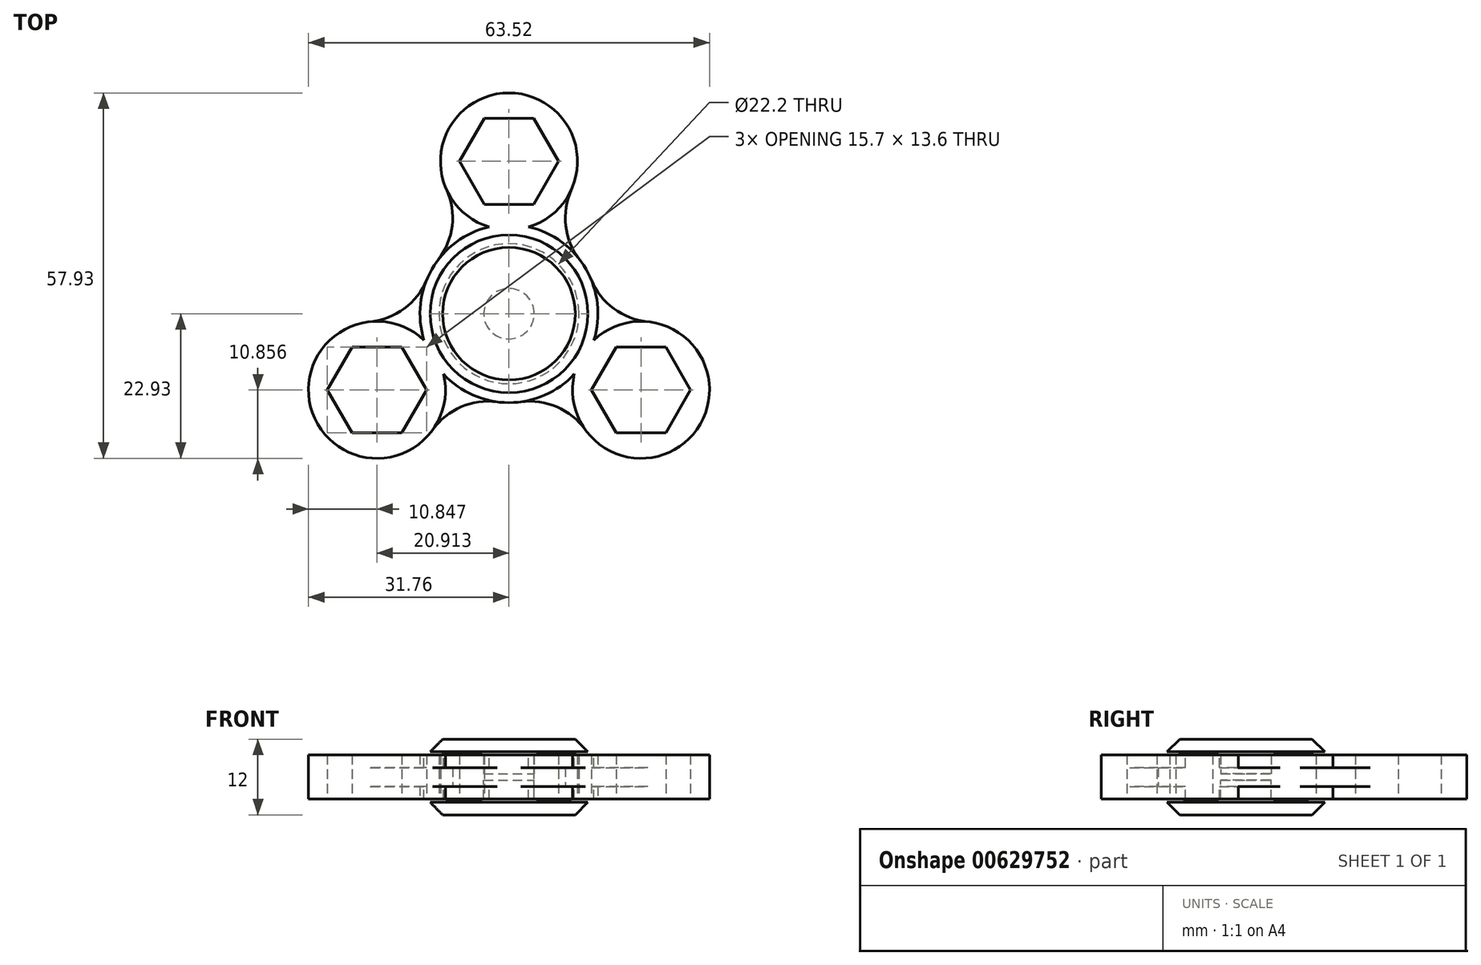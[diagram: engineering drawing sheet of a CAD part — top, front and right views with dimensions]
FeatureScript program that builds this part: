
annotation { "Feature Type Name" : "Feature", "Feature Type Description" : "" }
export const myFeature = defineFeature(function(context is Context, id is Id, definition is map)
    precondition{}
    {
        {
            var Q0;
            Q0=qCreatedBy(makeId("Top.planeOp"),FACE);
            var sketch = newSketch(context, id + "F0", { "sketchPlane" : qUnion([Q0])});
            skCircle(sketch, "E0", {"center": v(0, 0) * mm, "radius": 11.1 * mm});
            skCircle(sketch, "E1.cCircle", {"center": v(0, 24.15) * mm, "radius": 6.8 * mm, "construction": true});
            skLineSegment(sketch, "E1.0", {"start": v(3.93, 17.35) * mm, "end": v(-3.93, 17.35) * mm});
            skLineSegment(sketch, "E1.1", {"start": v(-3.93, 17.35) * mm, "end": v(-7.85, 24.15) * mm});
            skLineSegment(sketch, "E1.2", {"start": v(-7.85, 24.15) * mm, "end": v(-3.93, 30.95) * mm});
            skLineSegment(sketch, "E1.3", {"start": v(-3.93, 30.95) * mm, "end": v(3.93, 30.95) * mm});
            skLineSegment(sketch, "E1.4", {"start": v(3.93, 30.95) * mm, "end": v(7.85, 24.15) * mm});
            skLineSegment(sketch, "E1.5", {"start": v(7.85, 24.15) * mm, "end": v(3.93, 17.35) * mm});
            skPoint(sketch, "E1.0.midPoint", {"position": v(0, 17.35) * mm});
            skLineSegment(sketch, "E2", {"start": v(0, 0) * mm, "end": v(0, 35) * mm, "construction": true});
            skArc(sketch, "E3", {"start": v(-11.18, 8.6) * mm, "mid": v(-12.21, 7.05) * mm, "end": v(-13.03, 5.38) * mm});
            skArc(sketch, "E4", {"start": v(-11.18, 8.6) * mm, "mid": v(-9, 13.96) * mm, "end": v(-9.89, 19.68) * mm});
            skArc(sketch, "E5", {"start": v(9.89, 19.68) * mm, "mid": v(9, 13.96) * mm, "end": v(11.18, 8.6) * mm});
            skArc(sketch, "E6.trimOffspring", {"start": v(9.89, 19.68) * mm, "mid": v(0, 35) * mm, "end": v(-9.89, 19.68) * mm});
            skArc(sketch, "E7.1.0", {"start": v(-1.86, -13.98) * mm, "mid": v(-7.59, -14.77) * mm, "end": v(-12.1, -18.4) * mm});
            skArc(sketch, "E7.1.1", {"start": v(-21.99, -1.28) * mm, "mid": v(-30.31, -17.5) * mm, "end": v(-12.1, -18.4) * mm});
            skLineSegment(sketch, "E7.1.2", {"start": v(-13.06, -12.07) * mm, "end": v(-16.99, -18.87) * mm});
            skLineSegment(sketch, "E7.1.3", {"start": v(-16.99, -18.87) * mm, "end": v(-24.84, -18.87) * mm});
            skLineSegment(sketch, "E7.1.4", {"start": v(-24.84, -18.87) * mm, "end": v(-28.76, -12.07) * mm});
            skLineSegment(sketch, "E7.1.5", {"start": v(-28.76, -12.07) * mm, "end": v(-24.84, -5.27) * mm});
            skLineSegment(sketch, "E7.1.6", {"start": v(-24.84, -5.27) * mm, "end": v(-16.99, -5.27) * mm});
            skLineSegment(sketch, "E7.1.7", {"start": v(-16.99, -5.27) * mm, "end": v(-13.06, -12.07) * mm});
            skArc(sketch, "E7.1.8", {"start": v(-21.99, -1.28) * mm, "mid": v(-16.59, 0.81) * mm, "end": v(-13.03, 5.38) * mm});
            skArc(sketch, "E7.2.0", {"start": v(13.03, 5.38) * mm, "mid": v(16.59, 0.81) * mm, "end": v(21.99, -1.28) * mm});
            skArc(sketch, "E7.2.1", {"start": v(12.1, -18.4) * mm, "mid": v(30.31, -17.5) * mm, "end": v(21.99, -1.28) * mm});
            skLineSegment(sketch, "E7.2.2", {"start": v(16.99, -5.27) * mm, "end": v(24.84, -5.27) * mm});
            skLineSegment(sketch, "E7.2.3", {"start": v(24.84, -5.27) * mm, "end": v(28.76, -12.07) * mm});
            skLineSegment(sketch, "E7.2.4", {"start": v(28.76, -12.07) * mm, "end": v(24.84, -18.87) * mm});
            skLineSegment(sketch, "E7.2.5", {"start": v(24.84, -18.87) * mm, "end": v(16.99, -18.87) * mm});
            skLineSegment(sketch, "E7.2.6", {"start": v(16.99, -18.87) * mm, "end": v(13.06, -12.07) * mm});
            skLineSegment(sketch, "E7.2.7", {"start": v(13.06, -12.07) * mm, "end": v(16.99, -5.27) * mm});
            skArc(sketch, "E7.2.8", {"start": v(12.1, -18.4) * mm, "mid": v(7.59, -14.77) * mm, "end": v(1.86, -13.98) * mm});
            skArc(sketch, "E8.trimOffspring", {"start": v(-1.86, -13.98) * mm, "mid": v(0, -14.1) * mm, "end": v(1.86, -13.98) * mm});
            skArc(sketch, "E9.trimOffspring", {"start": v(13.03, 5.38) * mm, "mid": v(12.21, 7.05) * mm, "end": v(11.18, 8.6) * mm});
            skArc(sketch, "E10", {"start": v(-13.03, 5.38) * mm, "mid": v(-14.09, 0.64) * mm, "end": v(-13.47, -4.18) * mm});
            skArc(sketch, "E11", {"start": v(11.18, 8.6) * mm, "mid": v(7.6, 11.88) * mm, "end": v(3.11, 13.75) * mm});
            skArc(sketch, "E12", {"start": v(1.86, -13.98) * mm, "mid": v(6.49, -12.52) * mm, "end": v(10.35, -9.57) * mm});
            skArc(sketch, "E13", {"start": v(-12.1, -18.4) * mm, "mid": v(-10.27, -14.18) * mm, "end": v(-10.35, -9.57) * mm});
            skArc(sketch, "E14", {"start": v(-9.89, 19.68) * mm, "mid": v(-7.14, 15.98) * mm, "end": v(-3.11, 13.75) * mm});
            skArc(sketch, "E15", {"start": v(21.99, -1.28) * mm, "mid": v(17.41, -1.8) * mm, "end": v(13.47, -4.18) * mm});
            skLineSegment(sketch, "E16", {"start": v(0, 24.15) * mm, "end": v(5.43, 33.55) * mm, "construction": true});
            skArc(sketch, "E17.trimOffspring", {"start": v(-13.47, -4.18) * mm, "mid": v(-17.41, -1.8) * mm, "end": v(-21.99, -1.28) * mm});
            skArc(sketch, "E18.trimOffspring", {"start": v(10.35, -9.57) * mm, "mid": v(10.27, -14.18) * mm, "end": v(12.1, -18.4) * mm});
            skArc(sketch, "E19.trimOffspring", {"start": v(3.11, 13.75) * mm, "mid": v(7.14, 15.98) * mm, "end": v(9.89, 19.68) * mm});
            skArc(sketch, "E20.trimOffspring", {"start": v(-3.11, 13.75) * mm, "mid": v(-7.6, 11.88) * mm, "end": v(-11.18, 8.6) * mm});
            skArc(sketch, "E21.trimOffspring", {"start": v(-10.35, -9.57) * mm, "mid": v(-6.49, -12.52) * mm, "end": v(-1.86, -13.98) * mm});
            skArc(sketch, "E22.trimOffspring", {"start": v(13.47, -4.18) * mm, "mid": v(14.09, 0.64) * mm, "end": v(13.03, 5.38) * mm});
            skSolve(sketch);
        }
        {
            var Q0;
            {var subQ1=sQuery(id+"F0.wireOp",EDGE,"E7.1.1");Q0=makeQuery(id+"F0.imprint","IMPRINT",FACE,{"disambiguationData":[TD([[makeQuery(id+"F0.imprint","IMPRINT",EDGE,{"derivedFrom":subQ1}),1.0]])]});}
            var Q1;
            {var subQ0=sQuery(id+"F0.wireOp",EDGE,"E7.1.8");Q1=makeQuery(id+"F0.imprint","IMPRINT",FACE,{"disambiguationData":[TD([[makeQuery(id+"F0.imprint","IMPRINT",EDGE,{"derivedFrom":subQ0}),-1.0]])]});}
            var Q2;
            Q2=makeQuery(id+"F0.imprint","IMPRINT",FACE,{"disambiguationData":[TD([[makeQuery(id+"F0.imprint","IMPRINT",EDGE,{"derivedFrom":sQuery(id+"F0.wireOp",EDGE,"E0")}),-1.0]])]});
            var Q3;
            {var subQ0=sQuery(id+"F0.wireOp",EDGE,"E4");Q3=makeQuery(id+"F0.imprint","IMPRINT",FACE,{"disambiguationData":[TD([[makeQuery(id+"F0.imprint","IMPRINT",EDGE,{"derivedFrom":subQ0}),-1.0]])]});}
            var Q4;
            Q4=makeQuery(id+"F0.imprint","IMPRINT",FACE,{"disambiguationData":[TD([[makeQuery(id+"F0.imprint","IMPRINT",EDGE,{"derivedFrom":sQuery(id+"F0.wireOp",EDGE,"E1.0")}),1.0]])]});
            var Q5;
            {var subQ0=sQuery(id+"F0.wireOp",EDGE,"E7.1.0");Q5=makeQuery(id+"F0.imprint","IMPRINT",FACE,{"disambiguationData":[TD([[makeQuery(id+"F0.imprint","IMPRINT",EDGE,{"derivedFrom":subQ0}),-1.0]])]});}
            var Q6;
            {var subQ0=sQuery(id+"F0.wireOp",EDGE,"E7.2.0");Q6=makeQuery(id+"F0.imprint","IMPRINT",FACE,{"disambiguationData":[TD([[makeQuery(id+"F0.imprint","IMPRINT",EDGE,{"derivedFrom":subQ0}),-1.0]])]});}
            var Q7;
            {var subQ0=sQuery(id+"F0.wireOp",EDGE,"E7.2.8");Q7=makeQuery(id+"F0.imprint","IMPRINT",FACE,{"disambiguationData":[TD([[makeQuery(id+"F0.imprint","IMPRINT",EDGE,{"derivedFrom":subQ0}),-1.0]])]});}
            var Q8;
            {var subQ0=sQuery(id+"F0.wireOp",EDGE,"E7.2.1");Q8=makeQuery(id+"F0.imprint","IMPRINT",FACE,{"disambiguationData":[TD([[makeQuery(id+"F0.imprint","IMPRINT",EDGE,{"derivedFrom":subQ0}),1.0]])]});}
            var Q9;
            {var subQ0=sQuery(id+"F0.wireOp",EDGE,"E5");Q9=makeQuery(id+"F0.imprint","IMPRINT",FACE,{"disambiguationData":[TD([[makeQuery(id+"F0.imprint","IMPRINT",EDGE,{"derivedFrom":subQ0}),-1.0]])]});}
            var Q10;
            {var subQ4=sQuery(id+"F0.wireOp",EDGE,"E3");Q10=makeQuery(id+"F0.imprint","IMPRINT",FACE,{"disambiguationData":[TD([[makeQuery(id+"F0.imprint","IMPRINT",EDGE,{"derivedFrom":subQ4}),1.0]])]});}
            extrude(context, id + "F1", {"entities" : qUnion([Q0, Q1, Q2, Q3, Q4, Q5, Q6, Q7, Q8, Q9, Q10]), "endBound" : BoundingType.SYMMETRIC, "depth" : 3 * mm, "offsetDistance" : 25 * mm});
        }
        {
            var Q0;
            Q0=makeQuery(id+"F0.imprint","IMPRINT",FACE,{"disambiguationData":[TD([[makeQuery(id+"F0.imprint","IMPRINT",EDGE,{"derivedFrom":sQuery(id+"F0.wireOp",EDGE,"E0")}),-1.0]])]});
            var Q1;
            Q1=makeQuery(id+"F0.imprint","IMPRINT",FACE,{"disambiguationData":[TD([[makeQuery(id+"F0.imprint","IMPRINT",EDGE,{"derivedFrom":sQuery(id+"F0.wireOp",EDGE,"E1.0")}),1.0]])]});
            extrude(context, id + "F2", {"entities" : qUnion([Q0, Q1]), "operationType" : NewBodyOperationType.ADD, "endBound" : BoundingType.SYMMETRIC, "oppositeDirection" : true, "depth" : 7 * mm, "offsetDistance" : 25 * mm});
        }
        {
            var Q0;
            Q0=qCreatedBy(makeId("Right.planeOp"),FACE);
            var sketch = newSketch(context, id + "F3", { "sketchPlane" : qUnion([Q0])});
            skLineSegment(sketch, "E23", {"start": v(4, 0.5) * mm, "end": v(4, 3.5) * mm});
            skLineSegment(sketch, "E24", {"start": v(4, 0.5) * mm, "end": v(0, 0.5) * mm});
            skLineSegment(sketch, "E25", {"start": v(0, 0.5) * mm, "end": v(0, 6) * mm});
            skArc(sketch, "E26", {"start": v(12.5, 4) * mm, "mid": v(8.24, 3.87) * mm, "end": v(4, 3.5) * mm});
            skLineSegment(sketch, "E27", {"start": v(12.5, 4) * mm, "end": v(10.5, 6) * mm});
            skLineSegment(sketch, "E28", {"start": v(10.5, 6) * mm, "end": v(0, 6) * mm});
            skLineSegment(sketch, "E29", {"start": v(12.5, 4) * mm, "end": v(0, 4) * mm, "construction": true});
            skSolve(sketch);
        }
        {
            var Q0;
            Q0=makeQuery(id+"F3.imprint","IMPRINT",FACE,{"disambiguationData":[TD([[makeQuery(id+"F3.imprint","IMPRINT",EDGE,{"derivedFrom":sQuery(id+"F3.wireOp",EDGE,"E23")}),1.0]])]});
            var Q1;
            Q1=sQuery(id+"F3.wireOp",EDGE,"E25");
            revolve(context, id + "F4", {"surfaceOperationType" : NewSurfaceOperationType.NEW, "entities" : qUnion([Q0]), "axis" : qUnion([Q1]), "revolveType" : RevolveType.FULL});
        }
        {
            var Q0;
            Q0=makeQuery(id+"F4.opRevolve","SWEPT_BODY",BODY,{"disambiguationData":[OSD([sQuery(id+"F3.wireOp",EDGE,"E23"),sQuery(id+"F3.wireOp",EDGE,"E24"),sQuery(id+"F3.wireOp",EDGE,"E25"),sQuery(id+"F3.wireOp",EDGE,"E26"),sQuery(id+"F3.wireOp",EDGE,"E27"),sQuery(id+"F3.wireOp",EDGE,"E28")])]});
            var Q1;
            Q1=qCreatedBy(makeId("Top.planeOp"),FACE);
            mirror(context, id + "F5", {"entities" : qUnion([Q0]), "mirrorPlane" : qUnion([Q1])});
        }
    });
